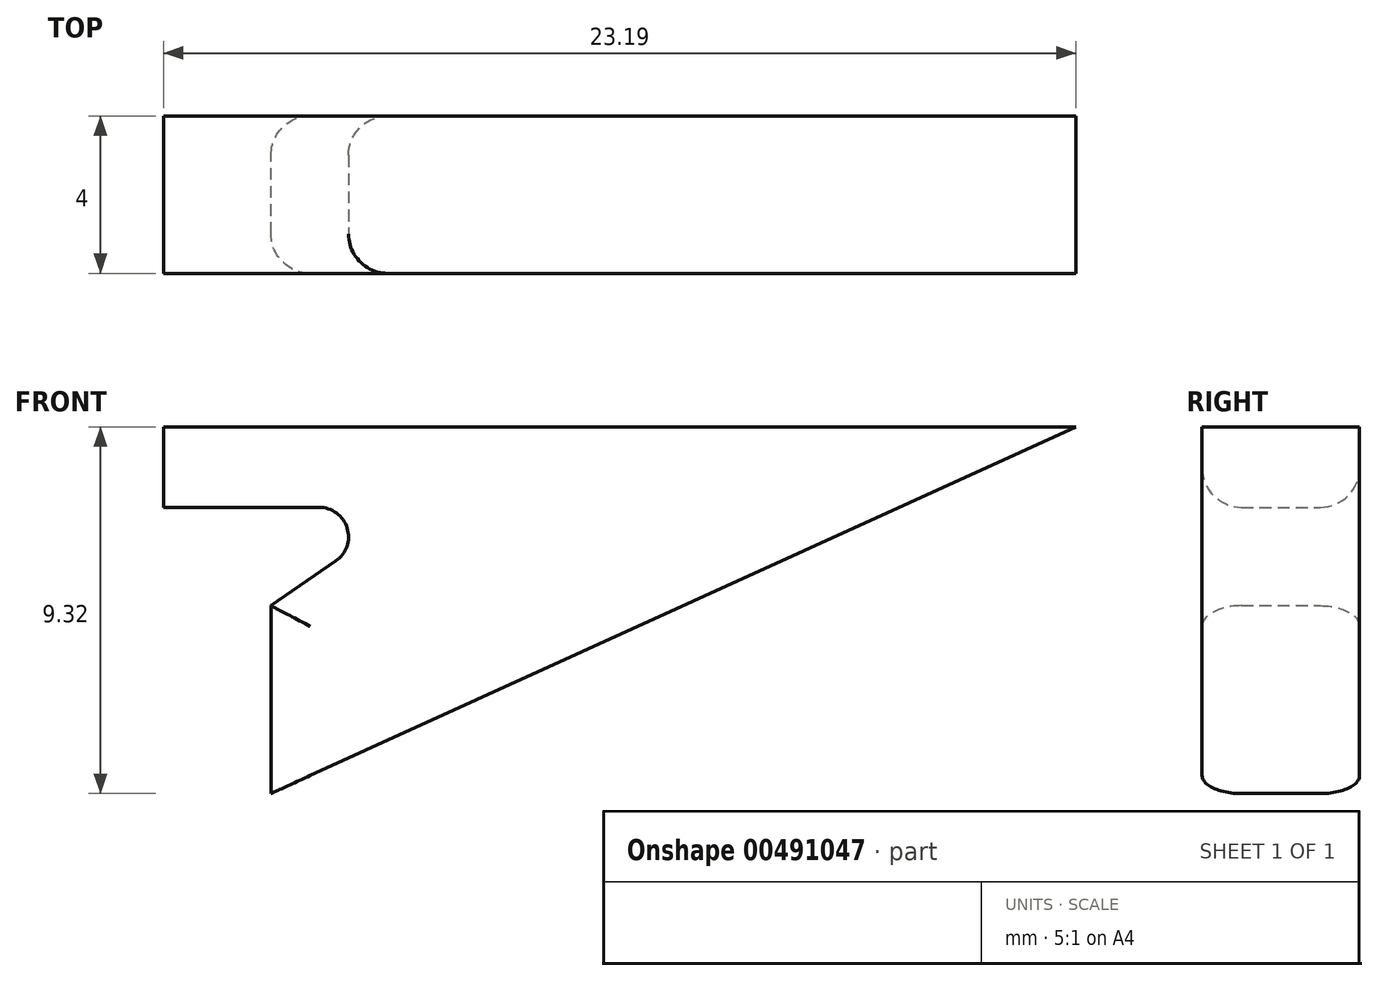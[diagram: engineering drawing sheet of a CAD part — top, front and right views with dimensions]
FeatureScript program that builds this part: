
annotation { "Feature Type Name" : "Feature", "Feature Type Description" : "" }
export const myFeature = defineFeature(function(context is Context, id is Id, definition is map)
    precondition{}
    {
        {
            var Q0;
            Q0=qCreatedBy(makeId("Front.planeOp"),FACE);
            var sketch = newSketch(context, id + "F0", { "sketchPlane" : qUnion([Q0])});
            skLineSegment(sketch, "E0", {"start": v(16.98, 2.62) * mm, "end": v(-3.48, -6.7) * mm});
            skLineSegment(sketch, "E1", {"start": v(-3.48, -6.7) * mm, "end": v(-3.48, -1.92) * mm});
            skLineSegment(sketch, "E2", {"start": v(-3.48, -1.92) * mm, "end": v(0.16, 0.58) * mm});
            skLineSegment(sketch, "E3", {"start": v(0.16, 0.58) * mm, "end": v(-6.2, 0.58) * mm});
            skLineSegment(sketch, "E4", {"start": v(-6.2, 0.58) * mm, "end": v(-6.2, 2.62) * mm});
            skLineSegment(sketch, "E5", {"start": v(-6.2, 2.62) * mm, "end": v(16.98, 2.62) * mm});
            skSolve(sketch);
        }
        {
            var Q0;
            Q0=makeQuery(id+"F0.imprint","IMPRINT",FACE,{"disambiguationData":[TD([[makeQuery(id+"F0.imprint","IMPRINT",EDGE,{"derivedFrom":sQuery(id+"F0.wireOp",EDGE,"E0")}),-1.0]])]});
            extrude(context, id + "F1", {"entities" : qUnion([Q0]), "depth" : 4 * mm});
        }
        {
            var Q0;
            Q0=makeQuery(id+"F1.opExtrude","SWEPT_EDGE",EDGE,{"disambiguationData":[OSD([sQuery(id+"F0.wireOp",EDGE,"E2"),sQuery(id+"F0.wireOp",EDGE,"E3")])]});
            fillet(context, id + "F2", {"entities" : qUnion([Q0]), "radius" : 0.75 * mm, "tangentPropagation" : true, "allowEdgeOverflow" : false});
        }
        {
            var Q0;
            Q0=makeQuery(id+"F1.opExtrude","CAP_EDGE",EDGE,{"disambiguationData":[OSD([sQuery(id+"F0.wireOp",EDGE,"E1")])],"isStart":false});
            var Q1;
            Q1=makeQuery(id+"F1.opExtrude","CAP_EDGE",EDGE,{"disambiguationData":[OSD([sQuery(id+"F0.wireOp",EDGE,"E2")])],"isStart":false});
            var Q2;
            Q2=makeQuery(id+"F1.opExtrude","CAP_EDGE",EDGE,{"disambiguationData":[OSD([sQuery(id+"F0.wireOp",EDGE,"E1")])],"isStart":true});
            var Q3;
            {var subQ0=sQuery(id+"F0.wireOp",EDGE,"E3");var subQ1=sQuery(id+"F0.wireOp",EDGE,"E2");Q3=makeQuery(id+"F2.opFillet","BLEND_EDGE",EDGE,{"blendedFrom":[makeQuery(id+"F1.opExtrude","SWEPT_EDGE",EDGE,{"disambiguationData":[OSD([subQ1,subQ0])]}),makeQuery(id+"F1.opExtrude","CAP_FACE",FACE,{"disambiguationData":[OSD([sQuery(id+"F0.wireOp",EDGE,"E0"),sQuery(id+"F0.wireOp",EDGE,"E1"),subQ1,subQ0,sQuery(id+"F0.wireOp",EDGE,"E4"),sQuery(id+"F0.wireOp",EDGE,"E5")])],"isStart":true})],"blendedInto":[makeQuery(id+"F1.opExtrude","CAP_FACE",FACE,{"disambiguationData":[OSD([sQuery(id+"F0.wireOp",EDGE,"E0"),sQuery(id+"F0.wireOp",EDGE,"E1"),subQ1,subQ0,sQuery(id+"F0.wireOp",EDGE,"E4"),sQuery(id+"F0.wireOp",EDGE,"E5")])],"isStart":true})]});}
            fillet(context, id + "F3", {"entities" : qUnion([Q0, Q1, Q2, Q3]), "radius" : 1 * mm, "tangentPropagation" : true, "allowEdgeOverflow" : false});
        }
    });
